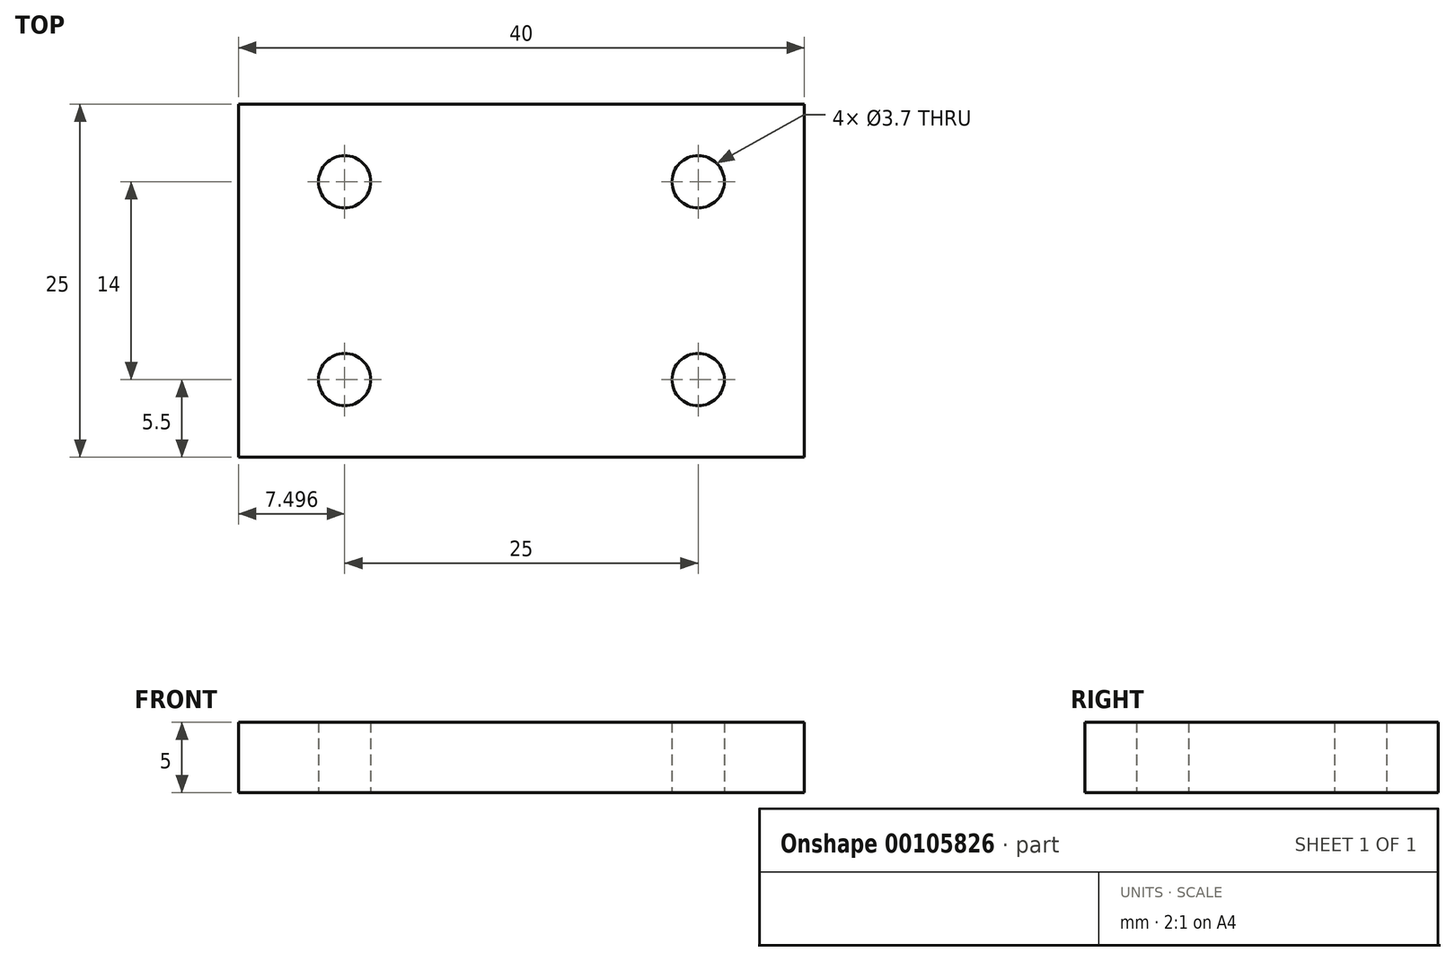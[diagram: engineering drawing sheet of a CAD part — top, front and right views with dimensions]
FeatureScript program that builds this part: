
annotation { "Feature Type Name" : "Feature", "Feature Type Description" : "" }
export const myFeature = defineFeature(function(context is Context, id is Id, definition is map)
    precondition{}
    {
        {
            var Q0;
            Q0=qCreatedBy(makeId("Top.planeOp"),FACE);
            var sketch = newSketch(context, id + "F0", { "sketchPlane" : qUnion([Q0])});
            skLineSegment(sketch, "E0.bottom", {"start": v(-28.8, 5.5) * mm, "end": v(11.2, 5.5) * mm});
            skLineSegment(sketch, "E0.top", {"start": v(-28.8, -19.5) * mm, "end": v(11.2, -19.5) * mm});
            skLineSegment(sketch, "E0.left", {"start": v(-28.8, 5.5) * mm, "end": v(-28.8, -19.5) * mm});
            skLineSegment(sketch, "E0.right", {"start": v(11.2, 5.5) * mm, "end": v(11.2, -19.5) * mm});
            skCircle(sketch, "E1", {"center": v(-21.3, 0) * mm, "radius": 1.85 * mm});
            skCircle(sketch, "E2", {"center": v(-21.3, -14) * mm, "radius": 1.85 * mm});
            skCircle(sketch, "E3", {"center": v(3.7, 0) * mm, "radius": 1.85 * mm});
            skCircle(sketch, "E4", {"center": v(3.7, -14) * mm, "radius": 1.85 * mm});
            skSolve(sketch);
        }
        {
            var Q0;
            Q0 = qSketchRegion(id + "F0", true);
            extrude(context, id + "F1", {"entities" : qUnion([Q0]), "depth" : 5 * mm});
        }
    });
